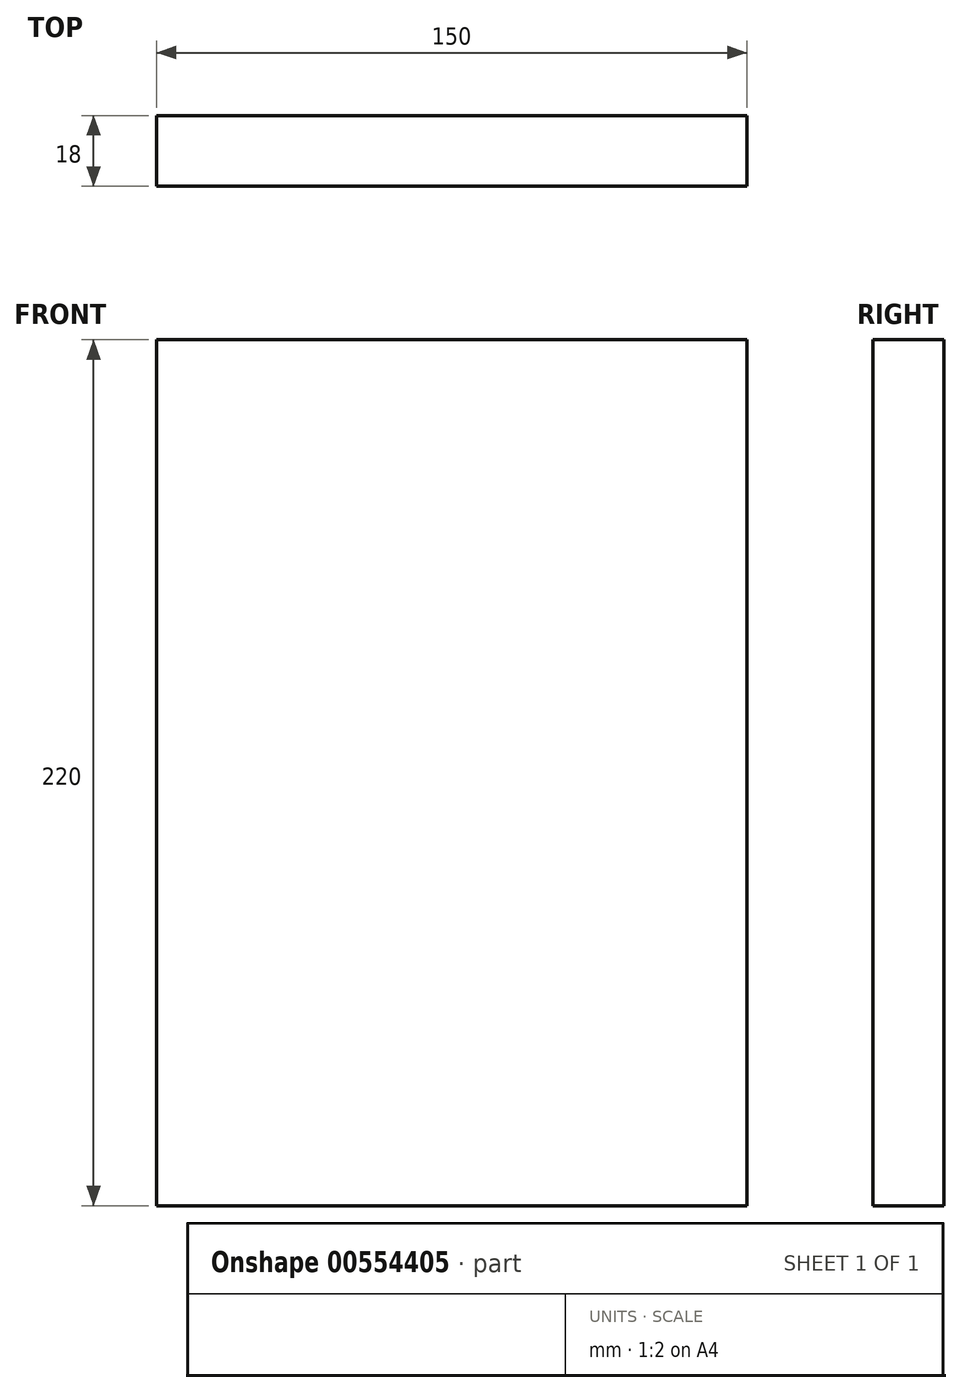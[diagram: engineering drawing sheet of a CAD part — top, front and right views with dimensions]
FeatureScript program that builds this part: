
annotation { "Feature Type Name" : "Feature", "Feature Type Description" : "" }
export const myFeature = defineFeature(function(context is Context, id is Id, definition is map)
    precondition{}
    {
        {
            var Q0;
            Q0=qCreatedBy(makeId("Front.planeOp"),FACE);
            var sketch = newSketch(context, id + "F0", { "sketchPlane" : qUnion([Q0])});
            skLineSegment(sketch, "E0.bottom", {"start": v(0, 0) * mm, "end": v(150, 0) * mm});
            skLineSegment(sketch, "E0.top", {"start": v(0, 220) * mm, "end": v(150, 220) * mm});
            skLineSegment(sketch, "E0.left", {"start": v(0, 0) * mm, "end": v(0, 220) * mm});
            skLineSegment(sketch, "E0.right", {"start": v(150, 0) * mm, "end": v(150, 220) * mm});
            skSolve(sketch);
        }
        {
            var Q0;
            Q0=makeQuery(id+"F0.imprint","IMPRINT",FACE,{"disambiguationData":[TD([[makeQuery(id+"F0.imprint","IMPRINT",EDGE,{"derivedFrom":sQuery(id+"F0.wireOp",EDGE,"E0.bottom")}),1.0]])]});
            extrude(context, id + "F1", {"entities" : qUnion([Q0]), "depth" : 18 * mm, "offsetDistance" : 25 * mm});
        }
    });
